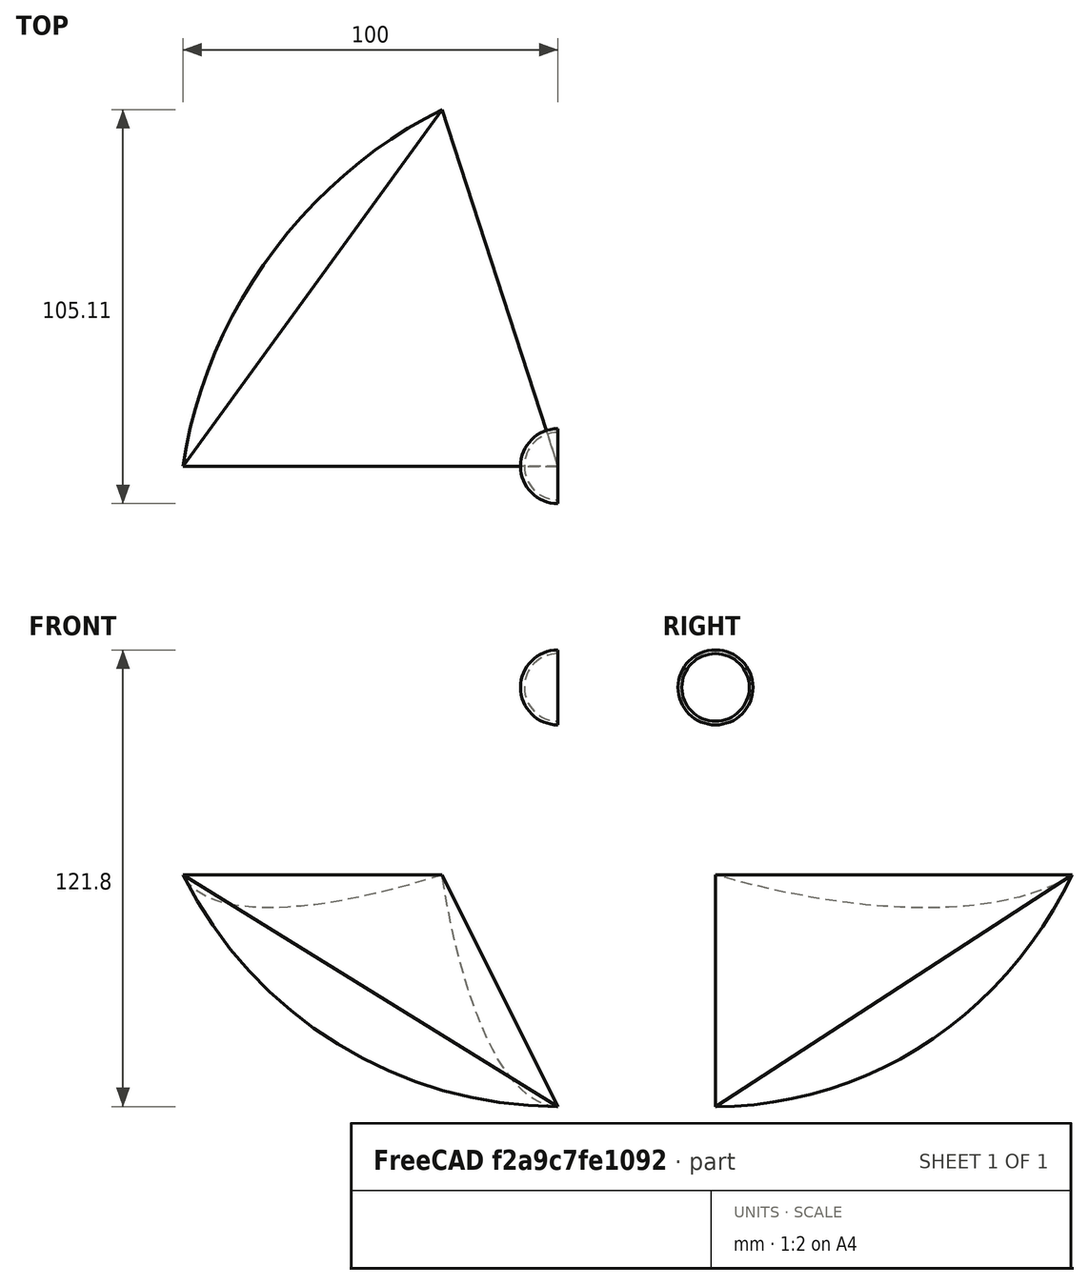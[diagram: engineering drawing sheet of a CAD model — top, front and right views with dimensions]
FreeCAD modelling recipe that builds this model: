
FCSTD DOCUMENT  (FreeCAD 0.19R24267 +99 (Git))
Label: test
License: All rights reserved
LicenseURL: http://en.wikipedia.org/wiki/All_rights_reserved
objects: PartDesign::SubtractiveBox×9, PartDesign::Body×3, PartDesign::Plane×3, PartDesign::AdditiveSphere×2, Part::Part2DObjectPython×2, PartDesign::SubtractiveSphere×1, Part::Vertex×1, App::Part×1, Spreadsheet::Sheet×1
note: 33 computed .brp shape members not serialized (recipe doc carries the construction recipe); baked Part::Feature solids carry a one-line shape summary decoded from their .brp

FEATURE [PartDesign::AdditiveSphere] Sphere
  Angle1 = -90
  Angle2 = 90
  Angle3 = 360
  AttacherType = Attacher::AttachEngine3D
  Radius = 10
FEATURE [PartDesign::SubtractiveSphere] Sphere001
  Angle1 = -90
  Angle2 = 90
  Angle3 = 360
  AttacherType = Attacher::AttachEngine3D
  BaseFeature = -> Sphere
  Radius = 9
FEATURE [PartDesign::SubtractiveBox] Box
  AttacherType = Attacher::AttachEngine3D
  AttachmentOffset = pos=(-10,0,-10) rot=(0,0,1;0rad)
  BaseFeature = -> Sphere001
  Height = 20
  Length = 20
  MapMode = 4
  Placement = pos=(0,-10,-10) rot=(0.57735,0.57735,0.57735;4.18879rad)
  Support = -> [YZ_Plane]
  Width = 20
FEATURE [PartDesign::Body] Body
  Group = -> [Sphere,Sphere001,Box]
  Origin = -> Origin
  Tip = -> Box
FEATURE [Part::Part2DObjectPython] Polygon  label="pentagon1"  # Draft 2D object (typed FeaturePython)
  Area = 0
  ChamferSize = 0
  DrawMode = 0
  FacesNumber = 5
  FilletRadius = 0
  MakeFace = false
  Placement = pos=(0,0,50) rot=(0,0,1;0rad)
  Radius = 100
  expr: .Placement.Base.z = <<Spreadsheet>>.hex_radius / 2
  expr: Radius = <<Spreadsheet>>.hex_radius
FEATURE [Part::Part2DObjectPython] Polygon001  label="pentagon0"  # Draft 2D object (typed FeaturePython)
  Area = 0
  ChamferSize = 0
  DrawMode = 0
  FacesNumber = 5
  FilletRadius = 0
  MakeFace = false
  Placement = pos=(0,0,-50) rot=(0,0,1;0.628319rad)
  Radius = 100
  expr: .Placement.Base.z = -<<Spreadsheet>>.hex_radius / 2
  expr: Radius = <<Spreadsheet>>.hex_radius
FEATURE [Part::Vertex] Vertex  label="center"
  AttacherType = Attacher::AttachEngine3D
  X = 0
  Y = 0
  Z = 0
FEATURE [PartDesign::Body] Body001
  Origin = -> Origin002
FEATURE [App::Part] Part
  Group = -> [Polygon001,Polygon,Vertex,Body001]
  Origin = -> Origin001
FEATURE [Spreadsheet::Sheet] Spreadsheet
  cells = A4=hex_radius; C4(hex_radius)==100mm; A5=sphere_radius; C5(sphere_radius)==hex_radius / 2 * sqrt(5)
FEATURE [PartDesign::Plane] DatumPlane
  Length = 449.471
  MapMode = 13
  Placement = pos=(-16.6667,51.2947,33.3333) rot=(0.865183,0.137031,0.482371;0.63451rad)
  ResizeMode = 0
  Support = -> [Vertex,Polygon]
  Width = 497.343
FEATURE [PartDesign::AdditiveSphere] Sphere002
  Angle1 = -90
  Angle2 = 90
  Angle3 = 360
  AttacherType = Attacher::AttachEngine3D
  Radius = 111.803
  expr: Radius = <<Spreadsheet>>.sphere_radius
FEATURE [PartDesign::SubtractiveBox] Box001
  AttacherType = Attacher::AttachEngine3D
  AttachmentOffset = pos=(-200,-200,0) rot=(0,0,1;0rad)
  BaseFeature = -> Sphere002
  Height = 400
  Length = 400
  MapMode = 5
  Placement = pos=(-154.305,-172.312,-71.8129) rot=(0.865183,0.137031,0.482371;0.63451rad)
  Support = -> [DatumPlane]
  Width = 400
FEATURE [PartDesign::SubtractiveBox] Box002
  AttacherType = Attacher::AttachEngine3D
  AttachmentOffset = pos=(-200,-200,0) rot=(0,0,1;0rad)
  BaseFeature = -> Box001
  Height = 400
  Length = 400
  MapMode = 13
  Placement = pos=(-298.829,30.1015,-138.48) rot=(0.472633,-0.240819,-0.847717;1.08239rad)
  Support = -> [Vertex,Polygon001]
  Width = 400
FEATURE [PartDesign::SubtractiveBox] Box003
  AttacherType = Attacher::AttachEngine3D
  AttachmentOffset = pos=(-200,-200,0) rot=(0,0,1;0rad)
  BaseFeature = -> Box002
  Height = 400
  Length = 400
  MapMode = 13
  Placement = pos=(-63.715,293.505,-138.48) rot=(-0.137906,0.270656,0.952747;4.04547rad)
  Support = -> [Vertex,Polygon001]
  Width = 400
FEATURE [PartDesign::SubtractiveBox] Box004
  AttacherType = Attacher::AttachEngine3D
  AttachmentOffset = pos=(-200,-200,0) rot=(0,0,1;0rad)
  BaseFeature = -> Box003
  Height = 400
  Length = 400
  MapMode = 13
  Placement = pos=(259.451,151.295,-138.48) rot=(0.043241,0.273011,0.961039;2.83948rad)
  Support = -> [Vertex,Polygon001]
  Width = 400
FEATURE [PartDesign::SubtractiveBox] Box005
  AttacherType = Attacher::AttachEngine3D
  AttachmentOffset = pos=(-200,-200,0) rot=(0,0,1;0rad)
  BaseFeature = -> Box004
  Height = 400
  Length = 400
  MapMode = 13
  Placement = pos=(224.065,-200,-138.48) rot=(0.263602,0.263602,0.927916;1.64554rad)
  Support = -> [Vertex,Polygon001]
  Width = 400
FEATURE [PartDesign::Plane] DatumPlane001
  Length = 343.954
  MapMode = 13
  Placement = pos=(-33.3333,-1.99e-13,-53.9345) rot=(1,0,0;1.5708rad)
  ResizeMode = 0
  Support = -> [Box005,Vertex]
  Width = 249.585
FEATURE [PartDesign::SubtractiveBox] Box006
  AttacherType = Attacher::AttachEngine3D
  AttachmentOffset = pos=(-200,-200,0) rot=(0,0,1;0rad)
  BaseFeature = -> Box005
  Height = 400
  Length = 400
  MapMode = 5
  Placement = pos=(-233.333,-1.1297e-12,-253.934) rot=(1,0,0;1.5708rad)
  Support = -> [DatumPlane001]
  Width = 400
FEATURE [PartDesign::SubtractiveBox] Box007
  AttacherType = Attacher::AttachEngine3D
  AttachmentOffset = pos=(-200,-200,0) rot=(0,0,1;0rad)
  BaseFeature = -> Box006
  Height = 400
  Length = 400
  MapMode = 13
  Placement = pos=(51.5028,-158.509,-253.934) rot=(0.456966,0.62896,0.62896;2.28433rad)
  Support = -> [Vertex,Box006,Polygon001]
  Width = 400
FEATURE [PartDesign::Plane] DatumPlane002
  Length = 494.452
  MapMode = 13
  Placement = pos=(-43.6339,31.7019,-70.6011) rot=(-0.434677,0.853102,0.288571;3.43357rad)
  ResizeMode = 0
  Support = -> [Box007]
  Width = 533.198
FEATURE [PartDesign::SubtractiveBox] Box008
  AttacherType = Attacher::AttachEngine3D
  AttachmentOffset = pos=(-100,-100,0) rot=(0,0,1;0rad)
  BaseFeature = -> Box007
  Height = 100
  Length = 200
  MapMode = 5
  Placement = pos=(-38.1235,-95.9084,-131.307) rot=(0.532353,0.271248,0.801888;1.1321rad)
  Support = -> [DatumPlane002]
  Width = 200
FEATURE [PartDesign::Body] Body002
  Group = -> [DatumPlane,Sphere002,Box001,Box002,Box003,Box004,Box005,DatumPlane001,Box006,Box007,DatumPlane002,Box008]
  Origin = -> Origin003
  Tip = -> Box008
